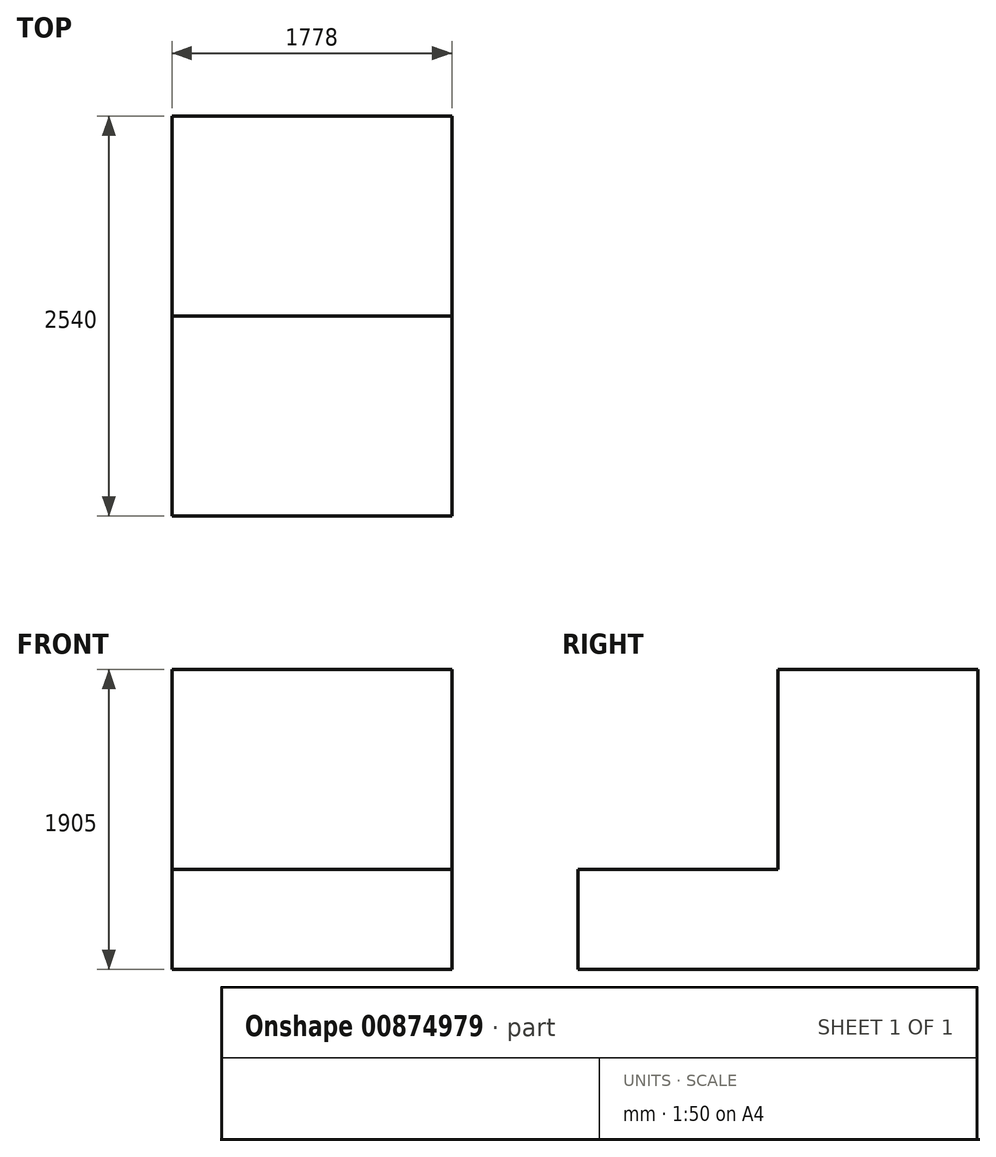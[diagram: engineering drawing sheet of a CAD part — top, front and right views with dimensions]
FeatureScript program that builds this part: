
annotation { "Feature Type Name" : "Feature", "Feature Type Description" : "" }
export const myFeature = defineFeature(function(context is Context, id is Id, definition is map)
    precondition{}
    {
        {
            var Q0;
            Q0=qCreatedBy(makeId("Right.planeOp"),FACE);
            var sketch = newSketch(context, id + "F0", { "sketchPlane" : qUnion([Q0])});
            skLineSegment(sketch, "E0", {"start": v(0, 0) * mm, "end": v(-2540, 0) * mm});
            skLineSegment(sketch, "E1", {"start": v(-2540, 0) * mm, "end": v(-2540, -635) * mm});
            skLineSegment(sketch, "E2", {"start": v(-2540, -635) * mm, "end": v(0, -635) * mm});
            skLineSegment(sketch, "E3", {"start": v(0, -635) * mm, "end": v(0, 0) * mm});
            skSolve(sketch);
        }
        {
            var Q0;
            Q0 = qSketchRegion(id + "F0", true);
            extrude(context, id + "F1", {"entities" : qUnion([Q0]), "depth" : 1778 * mm, "offsetDistance" : 25.4 * mm});
        }
        {
            var Q0;
            Q0=makeQuery(id+"F1.opExtrude","SWEPT_FACE",FACE,{"disambiguationData":[OSD([sQuery(id+"F0.wireOp",EDGE,"E0")])]});
            var sketch = newSketch(context, id + "F2", { "sketchPlane" : qUnion([Q0])});
            skLineSegment(sketch, "E4", {"start": v(0, -1270) * mm, "end": v(1778, -1270) * mm});
            skLineSegment(sketch, "E5", {"start": v(1778, -1270) * mm, "end": v(889, -1270) * mm});
            skLineSegment(sketch, "E6", {"start": v(889, -1270) * mm, "end": v(889, 0) * mm});
            skSolve(sketch);
        }
        {
            var Q0;
            {var subQ0=sQuery(id+"F2.wireOp",EDGE,"E4");Q0=makeQuery(id+"F2.imprint","IMPRINT",FACE,{"disambiguationData":[TD([[makeQuery(id+"F2.imprint","IMPRINT",EDGE,{"derivedFrom":subQ0}),1.0]])]});}
            extrude(context, id + "F3", {"entities" : qUnion([Q0]), "operationType" : NewBodyOperationType.ADD, "depth" : 1270 * mm, "offsetDistance" : 25.4 * mm});
        }
        {
            var Q0;
            Q0=makeQuery(id+"F1.opExtrude","SWEPT_FACE",FACE,{"disambiguationData":[OSD([sQuery(id+"F0.wireOp",EDGE,"E0")])]});
            var sketch = newSketch(context, id + "F4", { "sketchPlane" : qUnion([Q0])});
            skLineSegment(sketch, "E7", {"start": v(889, -1270) * mm, "end": v(1778, -1270) * mm});
            skLineSegment(sketch, "E8", {"start": v(1778, -1270) * mm, "end": v(1778, 0) * mm});
            skLineSegment(sketch, "E9", {"start": v(1778, 0) * mm, "end": v(889, 0) * mm});
            skLineSegment(sketch, "E10", {"start": v(889, 0) * mm, "end": v(889, -1270) * mm});
            skSolve(sketch);
        }
        {
            var Q0;
            Q0=makeQuery(id+"F4.imprint","IMPRINT",FACE,{"disambiguationData":[TD([[makeQuery(id+"F4.imprint","IMPRINT",EDGE,{"derivedFrom":sQuery(id+"F4.wireOp",EDGE,"E7")}),1.0]])]});
            extrude(context, id + "F5", {"entities" : qUnion([Q0]), "operationType" : NewBodyOperationType.ADD, "depth" : 965.2 * mm, "offsetDistance" : 25.4 * mm});
        }
    });
